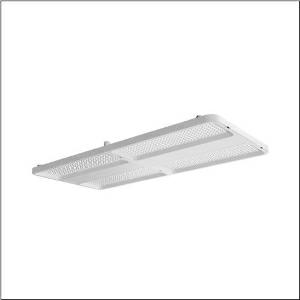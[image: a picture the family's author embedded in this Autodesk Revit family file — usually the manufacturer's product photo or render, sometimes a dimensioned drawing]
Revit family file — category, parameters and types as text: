
# Revit family: highbay_11_maxi_51hn12db4mba
name_source: partatom
category: Lighting Fixtures
units: mm (PartAtom-declared; Revit-internal decimal feet)

## family parameters
Cut with Voids When Loaded = No
Host = Face
Light Source = No
Part Type = Normal
Room Calculation Point = No
Round Connector Dimension = Use Diameter
Shared = No

## types (1)
- --- (1 x LED, 4620 lm, 22.4 W, 4000K)
    Apparent Load = 22 VA
    CIE Flux Codes = 87 98 100 100 100
    Color Rendering = 80
    Color Temperature = 4000K
    Default Elevation = 1800 mm
    Description = high bay luminaire Highbay 11 maxi; direct symmetric wide distribution, light control with lens of PMMA; UGR ≤ 22 (X = 4H | Y = 8H | S = 0.25H | reflection values 70/50/20); luminous flux: 30.000lm; light colour: 840, colour temperature: 4000K, MacAdam ≤ 2 SDCM (initial), colour rendering: CRI > 80; luminous efficacy: 204,8lm/W; rated service life: 100.000h (L95/B50) at AT= 25°C; control: DALI 2; luminaire connection: terminal, 5-pole, max. 2.5mm² (cable entry for one cable, Ø 8.5..16mm); mains connection: 230..240V, AC/DC 0/50..60Hz; connected load: 146,5W; protection rating (complete): IP40; insulation class (complete): insulation class I (protective earthing); protection symbol: D; impact resistance: IK08; certification: CE, ENEC, VDE, UKCA; luminaire for central battery installations according to DIN EN 60598-2-22, internal wiring halogen-free; luminaire corresponds to IFS (International Featured Standards) requirements for safety and quality in the food industry; LABS conformity tested according to VDMA 24364:2018-05; ball impact resistant only with use of appropriate mounting accessories; housing frame of high-performance plastic PA6, matt traffic white (RAL 9016); cover of PMMA; dimension (LxWxH): 946 x 442 x 72mm; permissible operating ambient temperature: -40..+60°C (reducing of maximum allowable ambient temperature of 5°C with ceiling mounting); packaging unit: 1 piece; (delivery without accessories; please order mounting accessories separately)
    Height = 72 mm  [stored 0.23622 ft]
    Lamp = 1 x LED
    Lamp Light Flux = 4620 lm
    Lamp Power = 22.4 W
    Lamp count = 1
    Length = 946 mm
    Luminous efficacy = 206 lm/W
    Manufacturer = Siteco
    ModVariant = No
    Model = 51HN12DB4MBA
    Mounting Place = Ceiling
    Mounting Type = Pendant
    Number of Poles = 1
    OnlyDefault = Yes
    Power Factor = 1
    Product Name = Highbay 11 maxi
    Product group = high bay luminaire
    ProductGroupID = 901
    Protection Class = Protection class I
    Protection Degree = IP 40
    RLX_Detail_Level = 1
    RLX_Emergency_Light_Flux = 0 lm
    RLX_Emergency_Type = 0
    RLX_Emergency_Type_DB = No
    RlxData = <blob elided: 127065 chars, md5=75f39900>
    Socket = socket
    Standby Power = 0 W
    System Light Flux = 4620 lm
    System Power = 22 W
    Type Comments = : DC mode (central or group accumulator) initial emergency light level
    Type Image = l_1376023.jpg
    URL = http://relux.com
    VarID = @adj_014109
    Voltage = 0 V
    Weight = 0.00 kg
    Width = 442 mm

note: [stored X ft] marks values corroborated as IEEE doubles in the binary element streams (Revit-internal decimal feet)

## geometry (parser evidence)
native form markers: Blend x4, Sweep x12
no freeform markers — native parametric forms only
